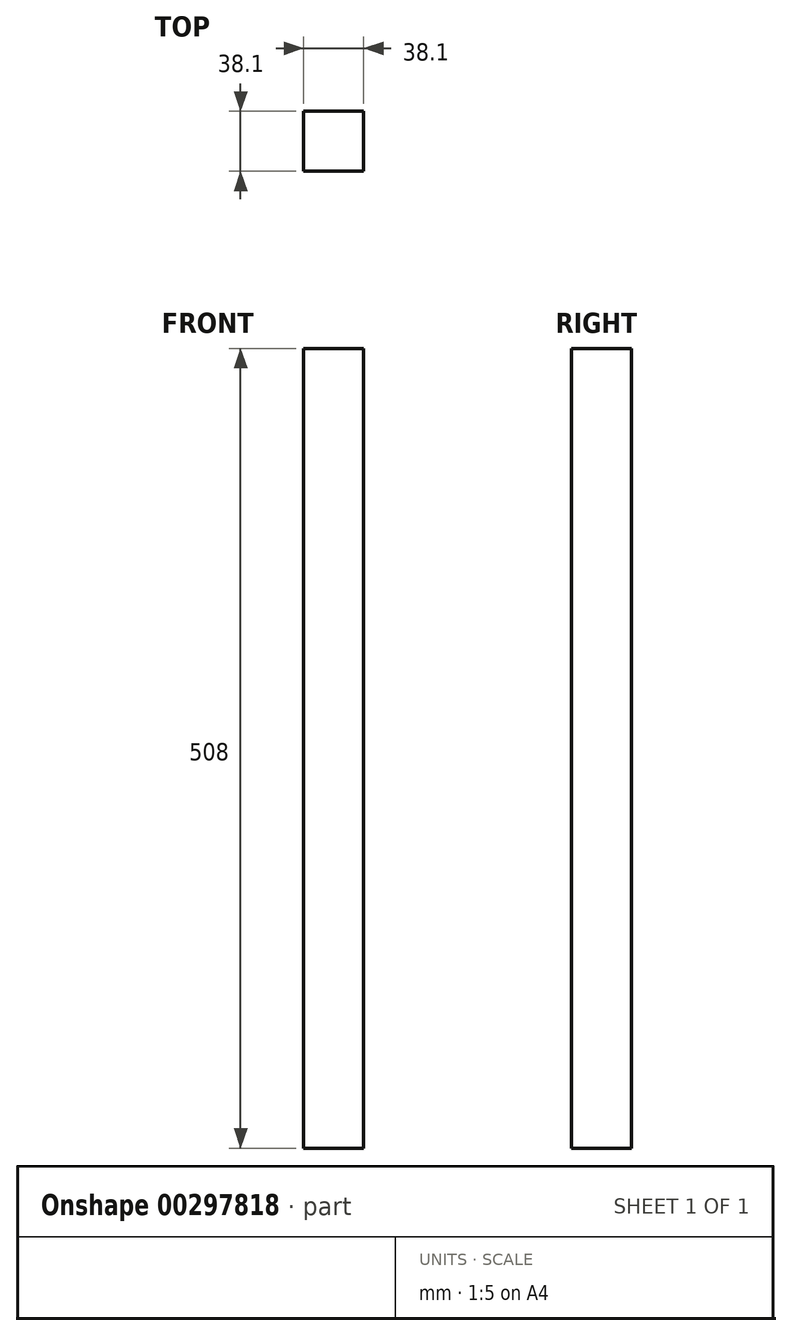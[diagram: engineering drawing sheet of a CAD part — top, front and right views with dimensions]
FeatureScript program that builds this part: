
annotation { "Feature Type Name" : "Feature", "Feature Type Description" : "" }
export const myFeature = defineFeature(function(context is Context, id is Id, definition is map)
    precondition{}
    {
        {
            var Q0;
            Q0=qCreatedBy(makeId("Top.planeOp"),FACE);
            var sketch = newSketch(context, id + "F0", { "sketchPlane" : qUnion([Q0])});
            skLineSegment(sketch, "E0.bottom", {"start": v(0, 0) * mm, "end": v(38.1, 0) * mm});
            skLineSegment(sketch, "E0.top", {"start": v(0, 38.1) * mm, "end": v(38.1, 38.1) * mm});
            skLineSegment(sketch, "E0.left", {"start": v(0, 0) * mm, "end": v(0, 38.1) * mm});
            skLineSegment(sketch, "E0.right", {"start": v(38.1, 0) * mm, "end": v(38.1, 38.1) * mm});
            skSolve(sketch);
        }
        {
            var Q0;
            Q0=makeQuery(id+"F0.imprint","IMPRINT",FACE,{"disambiguationData":[TD([[makeQuery(id+"F0.imprint","IMPRINT",EDGE,{"derivedFrom":sQuery(id+"F0.wireOp",EDGE,"E0.bottom")}),1.0]])]});
            extrude(context, id + "F1", {"entities" : qUnion([Q0]), "depth" : 508 * mm});
        }
    });
